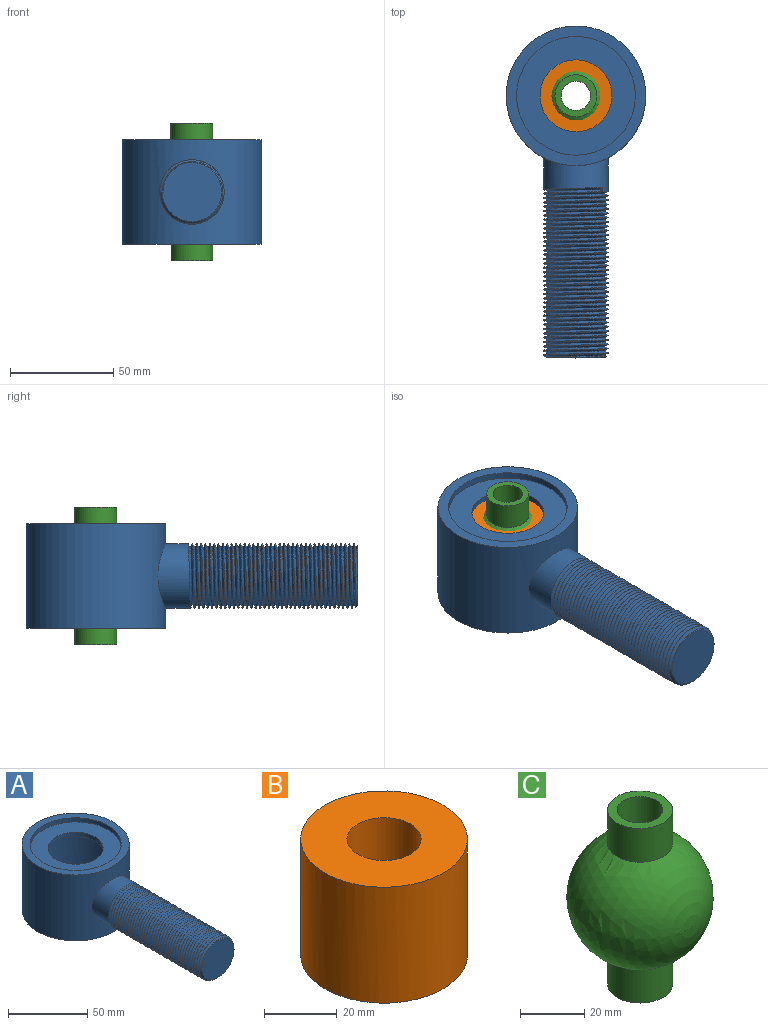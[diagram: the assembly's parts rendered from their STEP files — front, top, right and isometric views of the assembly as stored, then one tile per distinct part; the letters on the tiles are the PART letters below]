
ASSEMBLY  parts=3 mates=2
PART A: 56 faces, bbox 67.7x161.5x50.8 mm
  f0: cylinder r=28.77mm len=57.53mm, axis (0,0,-1), area 7029.6mm2, adj f51,f54
  f1: cylinder r=28.77mm len=57.53mm, axis (0,0,-1), area 573.8mm2, adj f5,f55
  f2: cone r=14.35mm half-angle=45deg, axis (0,1,0), area 91.9mm2, adj f7,f45,f46,f49
  f3: cylinder r=28.77mm len=57.53mm, axis (0,0,-1), area 430.4mm2, adj f6,f52
  f4: cylinder r=33.85mm len=67.69mm, axis (0,0,-1), area 10014.5mm2, adj f5,f6,f8
  f5: plane 67.69x67.69mm, normal (0,0,1), area 999.2mm2, adj f1,f4
  f6: plane 67.69x67.69mm, normal (0,0,-1), area 999.2mm2, adj f3,f4
  f7: plane 28.7x28.7mm, normal (0,-1,0), area 647mm2, adj f2
  f8: cylinder r=15.62mm len=31.24mm, axis (0,-1,0), area 1339.6mm2, adj f4,f9,f47,f48,f49
  f9: cylinder r=15.62mm len=31.24mm, axis (0,-1,0), area 16mm2, adj f8,f10,f48,f49
  f10: cylinder r=15.62mm len=31.24mm, axis (0,-1,0), area 16mm2, adj f9,f11,f48,f49
  f11: cylinder r=15.62mm len=31.24mm, axis (0,-1,0), area 16mm2, adj f10,f12,f48,f49
  f12: cylinder r=15.62mm len=31.24mm, axis (0,-1,0), area 16mm2, adj f11,f13,f48,f49
  f13: cylinder r=15.62mm len=31.24mm, axis (0,-1,0), area 16mm2, adj f12,f14,f48,f49
  f14: cylinder r=15.62mm len=31.24mm, axis (0,-1,0), area 16mm2, adj f13,f15,f48,f49
  f15: cylinder r=15.62mm len=31.24mm, axis (0,-1,0), area 16mm2, adj f14,f16,f48,f49
  f16: cylinder r=15.62mm len=31.24mm, axis (0,-1,0), area 16mm2, adj f15,f17,f48,f49
  f17: cylinder r=15.62mm len=31.24mm, axis (0,-1,0), area 16mm2, adj f16,f18,f48,f49
  f18: cylinder r=15.62mm len=31.24mm, axis (0,-1,0), area 16mm2, adj f17,f19,f48,f49
  f19: cylinder r=15.62mm len=31.24mm, axis (0,-1,0), area 16mm2, adj f18,f20,f48,f49
  f20: cylinder r=15.62mm len=31.24mm, axis (0,-1,0), area 16mm2, adj f19,f21,f48,f49
  f21: cylinder r=15.62mm len=31.24mm, axis (0,-1,0), area 16mm2, adj f20,f22,f48,f49
  f22: cylinder r=15.62mm len=31.24mm, axis (0,-1,0), area 16mm2, adj f21,f23,f48,f49
  f23: cylinder r=15.62mm len=31.24mm, axis (0,-1,0), area 16mm2, adj f22,f24,f48,f49
  f24: cylinder r=15.62mm len=31.24mm, axis (0,-1,0), area 16mm2, adj f23,f25,f48,f49
  f25: cylinder r=15.62mm len=31.24mm, axis (0,-1,0), area 16mm2, adj f24,f26,f48,f49
  f26: cylinder r=15.62mm len=31.24mm, axis (0,-1,0), area 16mm2, adj f25,f27,f48,f49
  f27: cylinder r=15.62mm len=31.24mm, axis (0,-1,0), area 16mm2, adj f26,f28,f48,f49
  f28: cylinder r=15.62mm len=31.24mm, axis (0,-1,0), area 16mm2, adj f27,f29,f48,f49
  f29: cylinder r=15.62mm len=31.24mm, axis (0,-1,0), area 16mm2, adj f28,f30,f48,f49
  f30: cylinder r=15.62mm len=31.24mm, axis (0,-1,0), area 16mm2, adj f29,f31,f48,f49
  f31: cylinder r=15.62mm len=31.24mm, axis (0,-1,0), area 16mm2, adj f30,f32,f48,f49
  f32: cylinder r=15.62mm len=31.24mm, axis (0,-1,0), area 16mm2, adj f31,f33,f48,f49
  f33: cylinder r=15.62mm len=31.24mm, axis (0,-1,0), area 16mm2, adj f32,f34,f48,f49
  f34: cylinder r=15.62mm len=31.24mm, axis (0,-1,0), area 16mm2, adj f33,f35,f48,f49
  f35: cylinder r=15.62mm len=31.24mm, axis (0,-1,0), area 16mm2, adj f34,f36,f48,f49
  f36: cylinder r=15.62mm len=31.24mm, axis (0,-1,0), area 16mm2, adj f35,f37,f48,f49
  f37: cylinder r=15.62mm len=31.24mm, axis (0,-1,0), area 16mm2, adj f36,f38,f48,f49
  f38: cylinder r=15.62mm len=31.24mm, axis (0,-1,0), area 16mm2, adj f37,f39,f48,f49
  f39: cylinder r=15.62mm len=31.24mm, axis (0,-1,0), area 16mm2, adj f38,f40,f48,f49
  f40: cylinder r=15.62mm len=31.24mm, axis (0,-1,0), area 16mm2, adj f39,f41,f48,f49
  f41: cylinder r=15.62mm len=31.24mm, axis (0,-1,0), area 16mm2, adj f40,f42,f48,f49
  f42: cylinder r=15.62mm len=31.24mm, axis (0,-1,0), area 16mm2, adj f41,f43,f48,f49
  f43: cylinder r=15.62mm len=31.24mm, axis (0,-1,0), area 16mm2, adj f42,f44,f48,f49
  f44: cylinder r=15.62mm len=31.24mm, axis (0,-1,0), area 16mm2, adj f43,f45,f48,f49
  f45: cylinder r=15.62mm len=31.24mm, axis (0,-1,0), area 12.6mm2, adj f2,f44,f48,f49
  f46: plane 1.69x1.24mm, normal (0,0,1), area 0.4mm2, adj f2,f48,f49
  f47: plane 1.96x1.37mm, normal (-0.59,0,0.81), area 1.7mm2, adj f8,f48,f49
  f48: bspline ~82.47x36.08mm, area 6967.3mm2, adj f8,f9,f10,f11,f12,f13,f14,f15
  f49: bspline ~82.47x36.08mm, area 6897.1mm2, adj f2,f8,f9,f10,f11,f12,f13,f14
  f50: cylinder r=17.43mm len=34.86mm, axis (0,0,-1), area 347.7mm2, adj f51,f52
  f51: plane 57.53x57.53mm, normal (0,0,1), area 1645mm2, adj f0,f50
  f52: plane 57.53x57.53mm, normal (0,0,-1), area 1645mm2, adj f3,f50
  f53: cylinder r=17.43mm len=34.86mm, axis (0,0,1), area 347.7mm2, adj f54,f55
  f54: plane 57.53x57.53mm, normal (0,0,-1), area 1645mm2, adj f0,f53
  f55: plane 57.53x57.53mm, normal (0,0,1), area 1645mm2, adj f1,f53
PART B: 4 faces, bbox 45.7x45.7x38.9 mm
  f0: plane 45.72x45.72mm, normal (0,0,-1), area 1317.4mm2, adj f2,f3
  f1: plane 45.72x45.72mm, normal (0,0,1), area 1317.4mm2, adj f2,f3
  f2: cylinder r=10.16mm len=38.89mm, axis (0,0,1), area 2482.9mm2, adj f0,f1
  f3: cylinder r=22.86mm len=45.72mm, axis (0,0,1), area 5586.4mm2, adj f0,f1
PART C: 6 faces, bbox 45.7x45.7x66.7 mm
  f0: cylinder r=7.14mm len=66.68mm, axis (0,0,1), area 2992.7mm2, adj f1,f4
  f1: plane 20.32x20.32mm, normal (0,0,1), area 164mm2, adj f0,f2
  f2: cylinder r=10.16mm len=20.32mm, axis (0,0,-1), area 820.9mm2, adj f1,f5
  f3: cylinder r=10.16mm len=20.32mm, axis (0,0,-1), area 820.9mm2, adj f4,f5
  f4: plane 20.32x20.32mm, normal (0,0,-1), area 164mm2, adj f0,f3
  f5: sphere r=22.86mm, area 5882.8mm2, adj f2,f3
PLACE A t=(-15.67,129.65,-46.67)mm
PLACE B t=(-15.67,129.65,-46.27)mm
PLACE C t=(-15.67,129.65,-46.67)mm fixed
MATE fastened A.f4 <-> B.f3  axis (0,0,-1) through (-15.67,129.65,-46.67)mm
MATE ball C.f0 <-> B.f2  axis (0,0,1) through (-15.67,129.65,-46.67)mm
